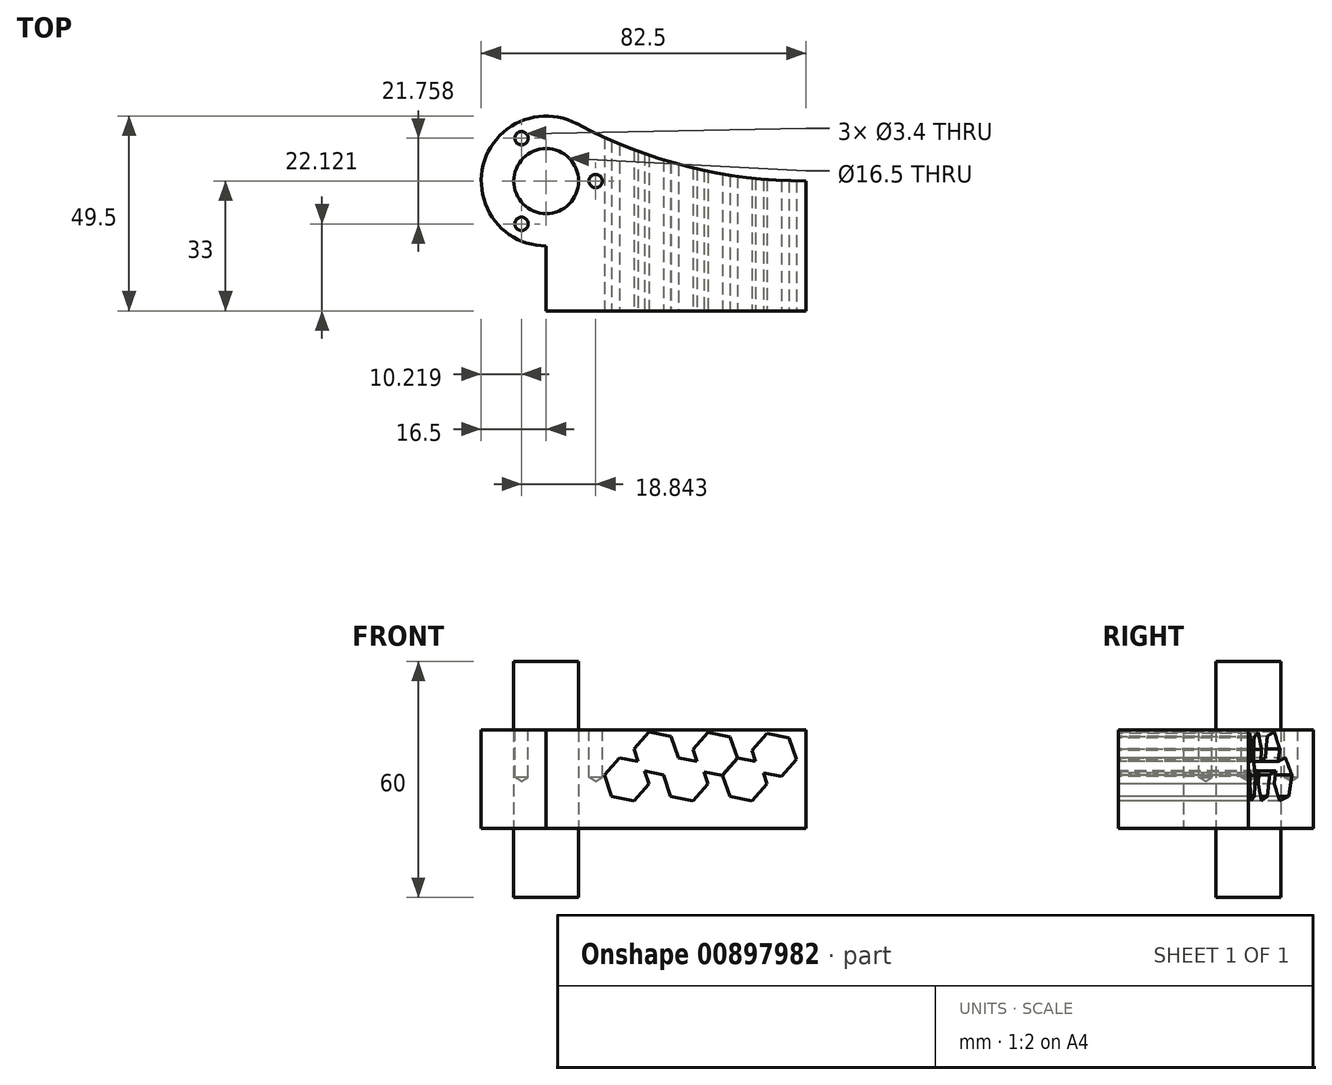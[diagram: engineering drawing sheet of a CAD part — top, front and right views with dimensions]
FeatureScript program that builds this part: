
annotation { "Feature Type Name" : "Feature", "Feature Type Description" : "" }
export const myFeature = defineFeature(function(context is Context, id is Id, definition is map)
    precondition{}
    {
        {
            var Q0;
            Q0=qCreatedBy(makeId("Top.planeOp"),FACE);
            var sketch = newSketch(context, id + "F0", { "sketchPlane" : qUnion([Q0])});
            skLineSegment(sketch, "E0.bottom", {"start": v(33, -16.5) * mm, "end": v(-33, -16.5) * mm});
            skLineSegment(sketch, "E0.top", {"start": v(33, 16.5) * mm, "end": v(-33, 16.5) * mm});
            skLineSegment(sketch, "E0.left", {"start": v(33, -16.5) * mm, "end": v(33, 16.5) * mm});
            skLineSegment(sketch, "E0.right", {"start": v(-33, -16.5) * mm, "end": v(-33, 16.5) * mm});
            skPoint(sketch, "E0.middle", {"position": v(0, 0) * mm});
            skCircle(sketch, "E1", {"center": v(-33, 16.5) * mm, "radius": 16.5 * mm});
            skArc(sketch, "E2", {"start": v(-25.24, 31.06) * mm, "mid": v(2.99, 20.2) * mm, "end": v(33, 16.5) * mm});
            skCircle(sketch, "E3", {"center": v(-33, 16.5) * mm, "radius": 8.25 * mm});
            skSolve(sketch);
        }
        {
            var Q0;
            {var subQ0=sQuery(id+"F0.wireOp",EDGE,"E1");var subQ4=sQuery(id+"F0.wireOp",EDGE,"E0.top");var subQ5=makeQuery(id+"F0.imprint","INTERSECT",VERTEX,{"derivedFrom":[subQ4,subQ0]});Q0=makeQuery(id+"F0.imprint","IMPRINT",FACE,{"disambiguationData":[TD([[makeQuery(id+"F0.imprint","IMPRINT",EDGE,{"disambiguationData":[TD([[subQ5,-1.0]])],"derivedFrom":subQ4}),-1.0]])]});}
            var Q1;
            {var subQ0=sQuery(id+"F0.wireOp",EDGE,"E1");var subQ1=sQuery(id+"F0.wireOp",EDGE,"E0.top");var subQ2=makeQuery(id+"F0.imprint","INTERSECT",VERTEX,{"derivedFrom":[subQ1,subQ0]});Q1=makeQuery(id+"F0.imprint","IMPRINT",FACE,{"disambiguationData":[TD([[makeQuery(id+"F0.imprint","IMPRINT",EDGE,{"disambiguationData":[TD([[subQ2,-1.0]])],"derivedFrom":subQ1}),1.0]])]});}
            var Q2;
            {var subQ5=sQuery(id+"F0.wireOp",EDGE,"E0.bottom");Q2=makeQuery(id+"F0.imprint","IMPRINT",FACE,{"disambiguationData":[TD([[makeQuery(id+"F0.imprint","IMPRINT",EDGE,{"derivedFrom":subQ5}),-1.0]])]});}
            var Q3;
            {var subQ0=sQuery(id+"F0.wireOp",EDGE,"E2");Q3=makeQuery(id+"F0.imprint","IMPRINT",FACE,{"disambiguationData":[TD([[makeQuery(id+"F0.imprint","IMPRINT",EDGE,{"derivedFrom":subQ0}),-1.0]])]});}
            extrude(context, id + "F1", {"entities" : qUnion([Q0, Q1, Q2, Q3]), "endBound" : BoundingType.SYMMETRIC, "depth" : 25 * mm, "offsetDistance" : 25 * mm});
        }
        {
            var Q0;
            {var subQ0=sQuery(id+"F0.wireOp",EDGE,"E0.right");var subQ1=sQuery(id+"F0.wireOp",EDGE,"E0.top");var subQ2=makeQuery(id+"F0.imprint","INTERSECT",VERTEX,{"derivedFrom":[subQ1,subQ0]});Q0=makeQuery(id+"F0.imprint","IMPRINT",FACE,{"disambiguationData":[TD([[makeQuery(id+"F0.imprint","IMPRINT",EDGE,{"disambiguationData":[TD([[subQ2,1.0]])],"derivedFrom":subQ1}),-1.0]])]});}
            var Q1;
            {var subQ0=sQuery(id+"F0.wireOp",EDGE,"E0.right");var subQ1=sQuery(id+"F0.wireOp",EDGE,"E0.top");var subQ2=makeQuery(id+"F0.imprint","INTERSECT",VERTEX,{"derivedFrom":[subQ1,subQ0]});Q1=makeQuery(id+"F0.imprint","IMPRINT",FACE,{"disambiguationData":[TD([[makeQuery(id+"F0.imprint","IMPRINT",EDGE,{"disambiguationData":[TD([[subQ2,1.0]])],"derivedFrom":subQ1}),1.0]])]});}
            extrude(context, id + "F2", {"entities" : qUnion([Q0, Q1]), "endBound" : BoundingType.SYMMETRIC, "depth" : 60 * mm, "offsetDistance" : 25 * mm});
        }
        {
            var Q0;
            Q0=makeQuery(id+"F1.opExtrude","SWEPT_FACE",FACE,{"disambiguationData":[OSD([sQuery(id+"F0.wireOp",EDGE,"E0.bottom")])]});
            var sketch = newSketch(context, id + "F3", { "sketchPlane" : qUnion([Q0])});
            skCircle(sketch, "E4.cCircle", {"center": v(-12.57, 0) * mm, "radius": 5 * mm, "construction": true});
            skLineSegment(sketch, "E4.0", {"start": v(-14.42, 5.47) * mm, "end": v(-8.76, 4.34) * mm});
            skLineSegment(sketch, "E4.1", {"start": v(-8.76, 4.34) * mm, "end": v(-6.9, -1.13) * mm});
            skLineSegment(sketch, "E4.2", {"start": v(-6.9, -1.13) * mm, "end": v(-10.71, -5.47) * mm});
            skLineSegment(sketch, "E4.3", {"start": v(-10.71, -5.47) * mm, "end": v(-16.38, -4.34) * mm});
            skLineSegment(sketch, "E4.4", {"start": v(-16.38, -4.34) * mm, "end": v(-18.23, 1.13) * mm});
            skLineSegment(sketch, "E4.5", {"start": v(-18.23, 1.13) * mm, "end": v(-14.42, 5.47) * mm});
            skPoint(sketch, "E4.0.midPoint", {"position": v(-11.6, 4.9) * mm});
            skLineSegment(sketch, "E5.1.0.0", {"start": v(6.24, 4.34) * mm, "end": v(8.1, -1.13) * mm});
            skLineSegment(sketch, "E5.1.0.1", {"start": v(8.1, -1.13) * mm, "end": v(4.29, -5.47) * mm});
            skPoint(sketch, "E5.1.0.2", {"position": v(3.4, 4.9) * mm});
            skLineSegment(sketch, "E5.1.0.3", {"start": v(4.29, -5.47) * mm, "end": v(-1.38, -4.34) * mm});
            skCircle(sketch, "E5.1.0.4", {"center": v(2.43, 0) * mm, "radius": 5 * mm, "construction": true});
            skLineSegment(sketch, "E5.1.0.5", {"start": v(-3.23, 1.13) * mm, "end": v(0.58, 5.47) * mm});
            skLineSegment(sketch, "E5.1.0.6", {"start": v(0.58, 5.47) * mm, "end": v(6.24, 4.34) * mm});
            skLineSegment(sketch, "E5.1.0.7", {"start": v(-1.38, -4.34) * mm, "end": v(-3.23, 1.13) * mm});
            skLineSegment(sketch, "E5.2.0.0", {"start": v(21.24, 4.34) * mm, "end": v(23.1, -1.13) * mm});
            skLineSegment(sketch, "E5.2.0.1", {"start": v(23.1, -1.13) * mm, "end": v(19.29, -5.47) * mm});
            skPoint(sketch, "E5.2.0.2", {"position": v(18.4, 4.9) * mm});
            skLineSegment(sketch, "E5.2.0.3", {"start": v(19.29, -5.47) * mm, "end": v(13.62, -4.34) * mm});
            skCircle(sketch, "E5.2.0.4", {"center": v(17.43, 0) * mm, "radius": 5 * mm, "construction": true});
            skLineSegment(sketch, "E5.2.0.5", {"start": v(11.77, 1.13) * mm, "end": v(15.58, 5.47) * mm});
            skLineSegment(sketch, "E5.2.0.6", {"start": v(15.58, 5.47) * mm, "end": v(21.24, 4.34) * mm});
            skLineSegment(sketch, "E5.2.0.7", {"start": v(13.62, -4.34) * mm, "end": v(11.77, 1.13) * mm});
            skLineSegment(sketch, "E5.direction1", {"start": v(-16.38, -4.34) * mm, "end": v(-1.38, -4.34) * mm, "construction": true});
            skLineSegment(sketch, "E6.1.0.0", {"start": v(-10.73, 7.74) * mm, "end": v(-6.92, 12.08) * mm});
            skLineSegment(sketch, "E6.1.0.1", {"start": v(-1.26, 10.96) * mm, "end": v(0.6, 5.49) * mm});
            skLineSegment(sketch, "E6.1.0.2", {"start": v(0.6, 5.49) * mm, "end": v(-3.22, 1.15) * mm});
            skCircle(sketch, "E6.1.0.3", {"center": v(-5.07, 6.62) * mm, "radius": 5 * mm, "construction": true});
            skLineSegment(sketch, "E6.1.0.4", {"start": v(-3.22, 1.15) * mm, "end": v(-8.88, 2.28) * mm});
            skLineSegment(sketch, "E6.1.0.5", {"start": v(-6.92, 12.08) * mm, "end": v(-1.26, 10.96) * mm});
            skPoint(sketch, "E6.1.0.6", {"position": v(-4.1, 11.52) * mm});
            skLineSegment(sketch, "E6.1.0.7", {"start": v(-8.88, 2.28) * mm, "end": v(-10.73, 7.74) * mm});
            skLineSegment(sketch, "E6.direction1", {"start": v(-16.38, -4.34) * mm, "end": v(-8.88, 2.28) * mm, "construction": true});
            skPoint(sketch, "E7.1.0.0", {"position": v(10.9, 11.31) * mm});
            skLineSegment(sketch, "E7.1.0.1", {"start": v(11.78, 0.94) * mm, "end": v(6.12, 2.07) * mm});
            skLineSegment(sketch, "E7.1.0.2", {"start": v(8.07, 11.88) * mm, "end": v(13.74, 10.75) * mm});
            skLineSegment(sketch, "E7.1.0.3", {"start": v(13.74, 10.75) * mm, "end": v(15.6, 5.28) * mm});
            skLineSegment(sketch, "E7.1.0.4", {"start": v(11.77, 0.92) * mm, "end": v(15.58, 5.26) * mm});
            skCircle(sketch, "E7.1.0.5", {"center": v(9.93, 6.4) * mm, "radius": 5 * mm, "construction": true});
            skPoint(sketch, "E7.1.0.6", {"position": v(3.4, 4.7) * mm});
            skLineSegment(sketch, "E7.1.0.7", {"start": v(6.12, 2.07) * mm, "end": v(4.27, 7.54) * mm});
            skLineSegment(sketch, "E7.1.0.8", {"start": v(4.27, 7.54) * mm, "end": v(8.07, 11.88) * mm});
            skLineSegment(sketch, "E7.1.0.9", {"start": v(15.6, 5.28) * mm, "end": v(11.78, 0.94) * mm});
            skPoint(sketch, "E7.2.0.0", {"position": v(25.9, 11.1) * mm});
            skLineSegment(sketch, "E7.2.0.1", {"start": v(26.78, 0.73) * mm, "end": v(21.12, 1.86) * mm});
            skLineSegment(sketch, "E7.2.0.2", {"start": v(23.07, 11.67) * mm, "end": v(28.73, 10.54) * mm});
            skLineSegment(sketch, "E7.2.0.3", {"start": v(28.73, 10.54) * mm, "end": v(30.59, 5.07) * mm});
            skLineSegment(sketch, "E7.2.0.4", {"start": v(26.77, 0.71) * mm, "end": v(30.57, 5.05) * mm});
            skCircle(sketch, "E7.2.0.5", {"center": v(24.93, 6.2) * mm, "radius": 5 * mm, "construction": true});
            skPoint(sketch, "E7.2.0.6", {"position": v(18.4, 4.49) * mm});
            skLineSegment(sketch, "E7.2.0.7", {"start": v(21.12, 1.86) * mm, "end": v(19.26, 7.33) * mm});
            skLineSegment(sketch, "E7.2.0.8", {"start": v(19.26, 7.33) * mm, "end": v(23.07, 11.67) * mm});
            skLineSegment(sketch, "E7.2.0.9", {"start": v(30.59, 5.07) * mm, "end": v(26.78, 0.73) * mm});
            skLineSegment(sketch, "E7.direction1", {"start": v(-11.6, 4.9) * mm, "end": v(3.4, 4.7) * mm, "construction": true});
            skSolve(sketch);
        }
        {
            var Q0;
            {var subQ0=sQuery(id+"F3.wireOp",EDGE,"E4.2");Q0=makeQuery(id+"F3.imprint","IMPRINT",FACE,{"disambiguationData":[TD([[makeQuery(id+"F3.imprint","IMPRINT",EDGE,{"derivedFrom":subQ0}),-1.0]])]});}
            var Q1;
            {var subQ1=sQuery(id+"F3.wireOp",EDGE,"E5.2.0.1");Q1=makeQuery(id+"F3.imprint","IMPRINT",FACE,{"disambiguationData":[TD([[makeQuery(id+"F3.imprint","IMPRINT",EDGE,{"derivedFrom":subQ1}),-1.0]])]});}
            var Q2;
            {var subQ4=sQuery(id+"F3.wireOp",EDGE,"E5.1.0.1");Q2=makeQuery(id+"F3.imprint","IMPRINT",FACE,{"disambiguationData":[TD([[makeQuery(id+"F3.imprint","IMPRINT",EDGE,{"derivedFrom":subQ4}),-1.0]])]});}
            var Q3;
            Q3=makeQuery(id+"F3.imprint","IMPRINT",FACE,{"disambiguationData":[TD([[makeQuery(id+"F3.imprint","IMPRINT",EDGE,{"derivedFrom":sQuery(id+"F3.wireOp",EDGE,"E7.1.0.2")}),-1.0]])]});
            var Q4;
            {var subQ12=sQuery(id+"F3.wireOp",EDGE,"E6.1.0.0");Q4=makeQuery(id+"F3.imprint","IMPRINT",FACE,{"disambiguationData":[TD([[makeQuery(id+"F3.imprint","IMPRINT",EDGE,{"derivedFrom":subQ12}),-1.0]])]});}
            var Q5;
            {var subQ0=sQuery(id+"F3.wireOp",EDGE,"E5.2.0.6");var subQ1=sQuery(id+"F3.wireOp",EDGE,"E5.2.0.0");var subQ2=makeQuery(id+"F3.imprint","INTERSECT",VERTEX,{"derivedFrom":[subQ1,subQ0]});Q5=makeQuery(id+"F3.imprint","IMPRINT",FACE,{"disambiguationData":[TD([[makeQuery(id+"F3.imprint","IMPRINT",EDGE,{"disambiguationData":[TD([[subQ2,-1.0]])],"derivedFrom":subQ1}),-1.0]])]});}
            var Q6;
            {var subQ0=sQuery(id+"F3.wireOp",EDGE,"E5.1.0.6");var subQ1=sQuery(id+"F3.wireOp",EDGE,"E5.1.0.5");var subQ2=makeQuery(id+"F3.imprint","INTERSECT",VERTEX,{"derivedFrom":[subQ1,subQ0]});Q6=makeQuery(id+"F3.imprint","IMPRINT",FACE,{"disambiguationData":[TD([[makeQuery(id+"F3.imprint","IMPRINT",EDGE,{"disambiguationData":[TD([[subQ2,1.0]])],"derivedFrom":subQ1}),-1.0]])]});}
            var Q7;
            {var subQ0=sQuery(id+"F3.wireOp",EDGE,"E4.1");var subQ1=sQuery(id+"F3.wireOp",EDGE,"E4.0");var subQ2=makeQuery(id+"F3.imprint","INTERSECT",VERTEX,{"derivedFrom":[subQ1,subQ0]});Q7=makeQuery(id+"F3.imprint","IMPRINT",FACE,{"disambiguationData":[TD([[makeQuery(id+"F3.imprint","IMPRINT",EDGE,{"disambiguationData":[TD([[subQ2,1.0]])],"derivedFrom":subQ1}),-1.0]])]});}
            var Q8;
            {var subQ0=sQuery(id+"F3.wireOp",EDGE,"E5.1.0.6");var subQ1=sQuery(id+"F3.wireOp",EDGE,"E5.1.0.0");var subQ2=makeQuery(id+"F3.imprint","INTERSECT",VERTEX,{"derivedFrom":[subQ1,subQ0]});Q8=makeQuery(id+"F3.imprint","IMPRINT",FACE,{"disambiguationData":[TD([[makeQuery(id+"F3.imprint","IMPRINT",EDGE,{"disambiguationData":[TD([[subQ2,-1.0]])],"derivedFrom":subQ1}),-1.0]])]});}
            var Q9;
            Q9=makeQuery(id+"F3.imprint","IMPRINT",FACE,{"disambiguationData":[TD([[makeQuery(id+"F3.imprint","IMPRINT",EDGE,{"derivedFrom":sQuery(id+"F3.wireOp",EDGE,"E7.2.0.2")}),-1.0]])]});
            extrude(context, id + "F4", {"entities" : qUnion([Q0, Q1, Q2, Q3, Q4, Q5, Q6, Q7, Q8, Q9]), "operationType" : NewBodyOperationType.REMOVE, "endBound" : BoundingType.THROUGH_ALL, "oppositeDirection" : true, "depth" : 25 * mm, "offsetDistance" : 25 * mm});
        }
        {
            var Q0;
            Q0=makeQuery(id+"F1.opExtrude","CAP_FACE",FACE,{"disambiguationData":[OSD([sQuery(id+"F0.wireOp",EDGE,"E0.bottom"),sQuery(id+"F0.wireOp",EDGE,"E0.left"),sQuery(id+"F0.wireOp",EDGE,"E0.right"),sQuery(id+"F0.wireOp",EDGE,"E1"),sQuery(id+"F0.wireOp",EDGE,"E2"),sQuery(id+"F0.wireOp",EDGE,"E3")])],"isStart":false});
            var sketch = newSketch(context, id + "F5", { "sketchPlane" : qUnion([Q0])});
            skLineSegment(sketch, "E8.0", {"start": v(33, 16.5) * mm, "end": v(-33, 16.5) * mm, "construction": true});
            skPoint(sketch, "E9", {"position": v(-20.44, 16.5) * mm});
            skPoint(sketch, "E10.1.0", {"position": v(-39.28, 27.38) * mm});
            skPoint(sketch, "E10.2.0", {"position": v(-39.28, 5.62) * mm});
            skPoint(sketch, "E10.center", {"position": v(-33, 16.5) * mm});
            skSolve(sketch);
        }
        {
            var Q0;
            Q0=sQuery(id+"F5.wireOp",VERTEX,"E9");
            var Q1;
            Q1=sQuery(id+"F5.wireOp",VERTEX,"E10.1.0");
            var Q2;
            Q2=sQuery(id+"F5.wireOp",VERTEX,"E10.2.0");
            var Q3;
            Q3=makeQuery(id+"F2.opExtrude","SWEPT_BODY",BODY,{"disambiguationData":[OSD([sQuery(id+"F0.wireOp",EDGE,"E3")])]});
            var Q4;
            Q4=makeQuery(id+"F4.boolean.opBoolean","SPLIT",BODY,{"disambiguationData":[OD(0.0)],"derivedFrom":makeQuery(id+"F1.opExtrude","SWEPT_BODY",BODY,{"disambiguationData":[OSD([sQuery(id+"F0.wireOp",EDGE,"E0.bottom"),sQuery(id+"F0.wireOp",EDGE,"E0.left"),sQuery(id+"F0.wireOp",EDGE,"E0.right"),sQuery(id+"F0.wireOp",EDGE,"E1"),sQuery(id+"F0.wireOp",EDGE,"E2"),sQuery(id+"F0.wireOp",EDGE,"E3")])]})});
            var Q5;
            Q5=makeQuery(id+"F4.boolean.opBoolean","SPLIT",BODY,{"disambiguationData":[OD(1.0)],"derivedFrom":makeQuery(id+"F1.opExtrude","SWEPT_BODY",BODY,{"disambiguationData":[OSD([sQuery(id+"F0.wireOp",EDGE,"E0.bottom"),sQuery(id+"F0.wireOp",EDGE,"E0.left"),sQuery(id+"F0.wireOp",EDGE,"E0.right"),sQuery(id+"F0.wireOp",EDGE,"E1"),sQuery(id+"F0.wireOp",EDGE,"E2"),sQuery(id+"F0.wireOp",EDGE,"E3")])]})});
            hole(context, id + "F6", {"style" : HoleStyle.SIMPLE, "endStyle" : HoleEndStyle.BLIND, "standardTappedOrClearance" : lookupTablePath({ "fit" : "Normal", "standard" : "ISO", "size" : "M3", "type" : "Clearance" }), "standardBlindInLast" : lookupTablePath({ "fit" : "Normal", "standard" : "ISO", "size" : "M3", "type" : "Clearance" }), "holeDiameter" : 3.4 * mm, "majorDiameter" : 5 * mm, "holeDepth" : 12 * mm, "isTappedThrough" : true, "tappedDepth" : 12 * mm, "tapClearance" : 3, "locations" : qUnion([Q0, Q1, Q2]), "scope" : qUnion([Q3, Q4, Q5])});
        }
    });
